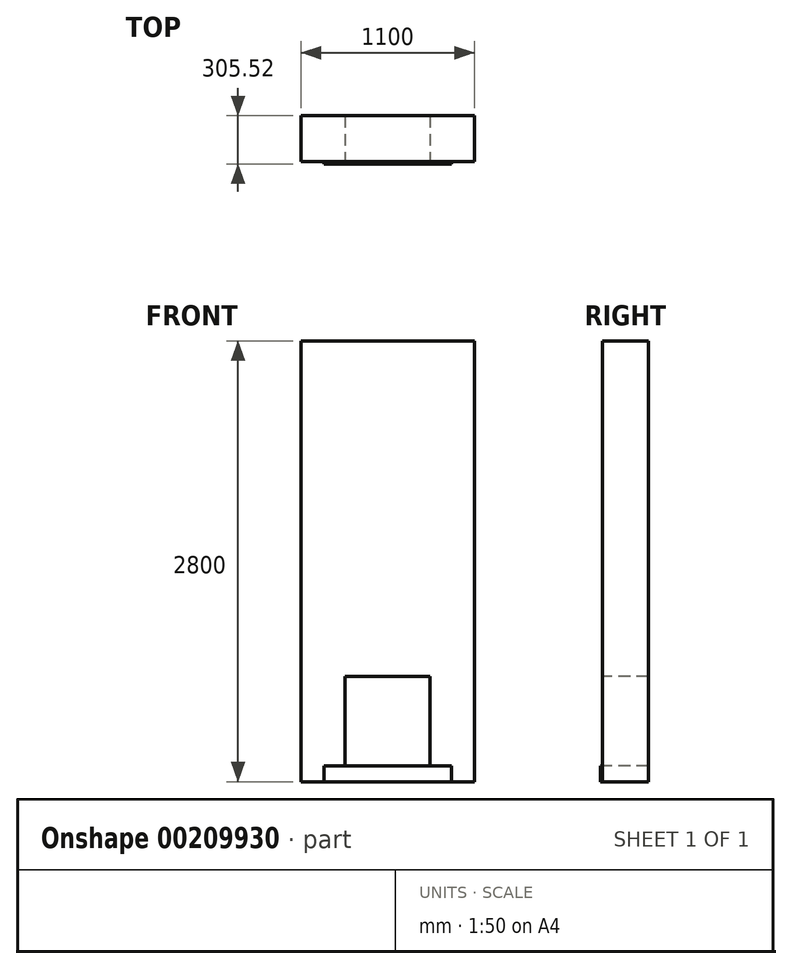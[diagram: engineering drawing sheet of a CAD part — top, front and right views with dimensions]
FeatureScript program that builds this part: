
annotation { "Feature Type Name" : "Feature", "Feature Type Description" : "" }
export const myFeature = defineFeature(function(context is Context, id is Id, definition is map)
    precondition{}
    {
        {
            var Q0;
            Q0=qCreatedBy(makeId("Front.planeOp"),FACE);
            var sketch = newSketch(context, id + "F0", { "sketchPlane" : qUnion([Q0])});
            skLineSegment(sketch, "E0.bottom", {"start": v(-550, 0) * mm, "end": v(550, 0) * mm});
            skLineSegment(sketch, "E0.top", {"start": v(-550, 2800) * mm, "end": v(550, 2800) * mm});
            skLineSegment(sketch, "E0.left", {"start": v(-550, 0) * mm, "end": v(-550, 2800) * mm});
            skLineSegment(sketch, "E0.right", {"start": v(550, 0) * mm, "end": v(550, 2800) * mm});
            skSolve(sketch);
        }
        {
            var Q0;
            Q0=makeQuery(id+"F0.imprint","IMPRINT",FACE,{"disambiguationData":[TD([[makeQuery(id+"F0.imprint","IMPRINT",EDGE,{"derivedFrom":sQuery(id+"F0.wireOp",EDGE,"E0.bottom")}),1.0]])]});
            extrude(context, id + "F4", {"entities" : qUnion([Q0]), "oppositeDirection" : true, "depth" : 290.52 * mm});
        }
        {
            var Q0;
            Q0=makeQuery(id+"F4.opExtrude","CAP_FACE",FACE,{"disambiguationData":[OSD([sQuery(id+"F0.wireOp",EDGE,"E0.bottom"),sQuery(id+"F0.wireOp",EDGE,"E0.top"),sQuery(id+"F0.wireOp",EDGE,"E0.left"),sQuery(id+"F0.wireOp",EDGE,"E0.right")])],"isStart":true});
            var sketch = newSketch(context, id + "F1", { "sketchPlane" : qUnion([Q0])});
            skLineSegment(sketch, "E1.bottom", {"start": v(-405, 0) * mm, "end": v(405, 0) * mm});
            skLineSegment(sketch, "E1.top", {"start": v(-405, 100) * mm, "end": v(405, 100) * mm});
            skLineSegment(sketch, "E1.left", {"start": v(-405, 0) * mm, "end": v(-405, 100) * mm});
            skLineSegment(sketch, "E1.right", {"start": v(405, 0) * mm, "end": v(405, 100) * mm});
            skSolve(sketch);
        }
        {
            var Q0;
            Q0=makeQuery(id+"F1.imprint","IMPRINT",FACE,{"disambiguationData":[TD([[makeQuery(id+"F1.imprint","IMPRINT",EDGE,{"derivedFrom":sQuery(id+"F1.wireOp",EDGE,"E1.bottom")}),1.0]])]});
            extrude(context, id + "F2", {"entities" : qUnion([Q0]), "operationType" : NewBodyOperationType.ADD, "depth" : 15 * mm});
        }
        {
            var Q0;
            Q0=makeQuery(id+"F4.opExtrude","CAP_FACE",FACE,{"disambiguationData":[OSD([sQuery(id+"F0.wireOp",EDGE,"E0.bottom"),sQuery(id+"F0.wireOp",EDGE,"E0.top"),sQuery(id+"F0.wireOp",EDGE,"E0.left"),sQuery(id+"F0.wireOp",EDGE,"E0.right")])],"isStart":true});
            var sketch = newSketch(context, id + "F3", { "sketchPlane" : qUnion([Q0])});
            skLineSegment(sketch, "E2.bottom", {"start": v(-270, 100) * mm, "end": v(270, 100) * mm});
            skLineSegment(sketch, "E2.top", {"start": v(-270, 670) * mm, "end": v(270, 670) * mm});
            skLineSegment(sketch, "E2.left", {"start": v(-270, 100) * mm, "end": v(-270, 670) * mm});
            skLineSegment(sketch, "E2.right", {"start": v(270, 100) * mm, "end": v(270, 670) * mm});
            skLineSegment(sketch, "E3", {"start": v(0, 973.17) * mm, "end": v(0, 2181.87) * mm, "construction": true});
            skLineSegment(sketch, "E4", {"start": v(0, 2181.87) * mm, "end": v(0, 973.17) * mm, "construction": true});
            skLineSegment(sketch, "E5", {"start": v(0, 973.17) * mm, "end": v(0, 0) * mm, "construction": true});
            skSolve(sketch);
        }
        {
            var Q0;
            Q0=makeQuery(id+"F3.imprint","IMPRINT",FACE,{"disambiguationData":[TD([[makeQuery(id+"F3.imprint","IMPRINT",EDGE,{"derivedFrom":sQuery(id+"F3.wireOp",EDGE,"E2.bottom")}),1.0]])]});
            extrude(context, id + "F5", {"entities" : qUnion([Q0]), "operationType" : NewBodyOperationType.REMOVE, "oppositeDirection" : true, "depth" : 300 * mm});
        }
    });
